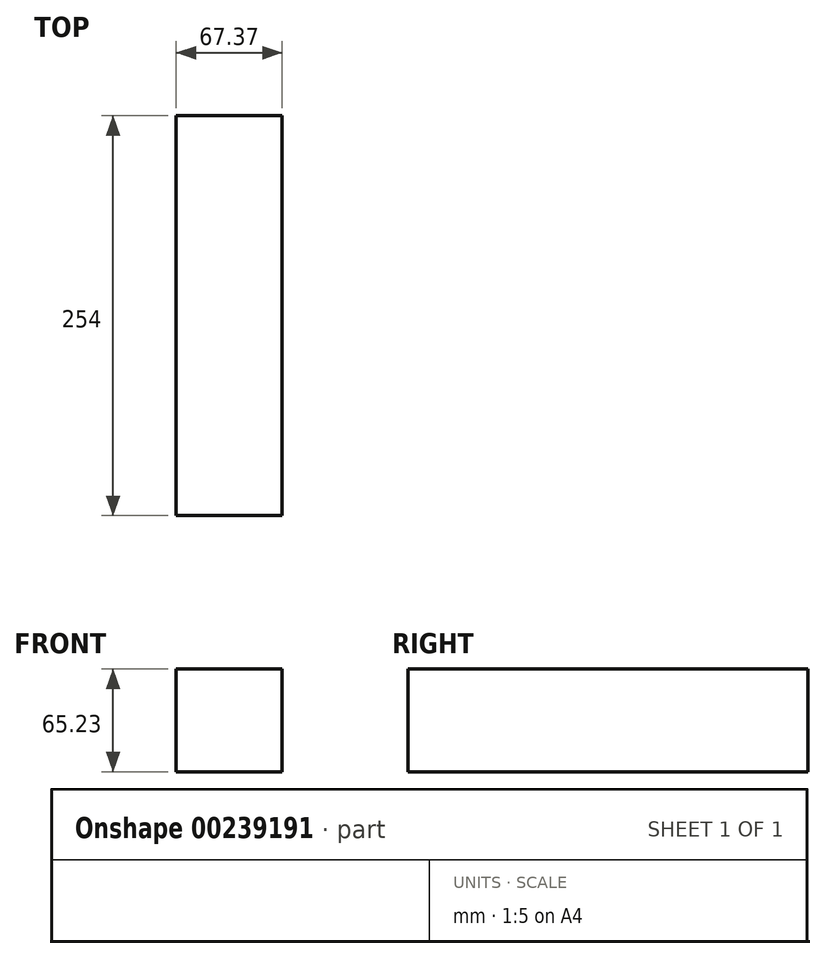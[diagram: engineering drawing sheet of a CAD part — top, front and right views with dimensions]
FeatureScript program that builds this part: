
annotation { "Feature Type Name" : "Feature", "Feature Type Description" : "" }
export const myFeature = defineFeature(function(context is Context, id is Id, definition is map)
    precondition{}
    {
        {
            var Q0;
            Q0=qCreatedBy(makeId("Front.planeOp"),FACE);
            var sketch = newSketch(context, id + "F0", { "sketchPlane" : qUnion([Q0])});
            skLineSegment(sketch, "E0.bottom", {"start": v(-32.51, 21.45) * mm, "end": v(34.86, 21.45) * mm});
            skLineSegment(sketch, "E0.top", {"start": v(-32.51, -43.78) * mm, "end": v(34.86, -43.78) * mm});
            skLineSegment(sketch, "E0.left", {"start": v(-32.51, 21.45) * mm, "end": v(-32.51, -43.78) * mm});
            skLineSegment(sketch, "E0.right", {"start": v(34.86, 21.45) * mm, "end": v(34.86, -43.78) * mm});
            skSolve(sketch);
        }
        {
            var Q0;
            Q0 = qSketchRegion(id + "F0", true);
            extrude(context, id + "F1", {"entities" : qUnion([Q0]), "endBound" : BoundingType.SYMMETRIC, "depth" : 254 * mm});
        }
    });
